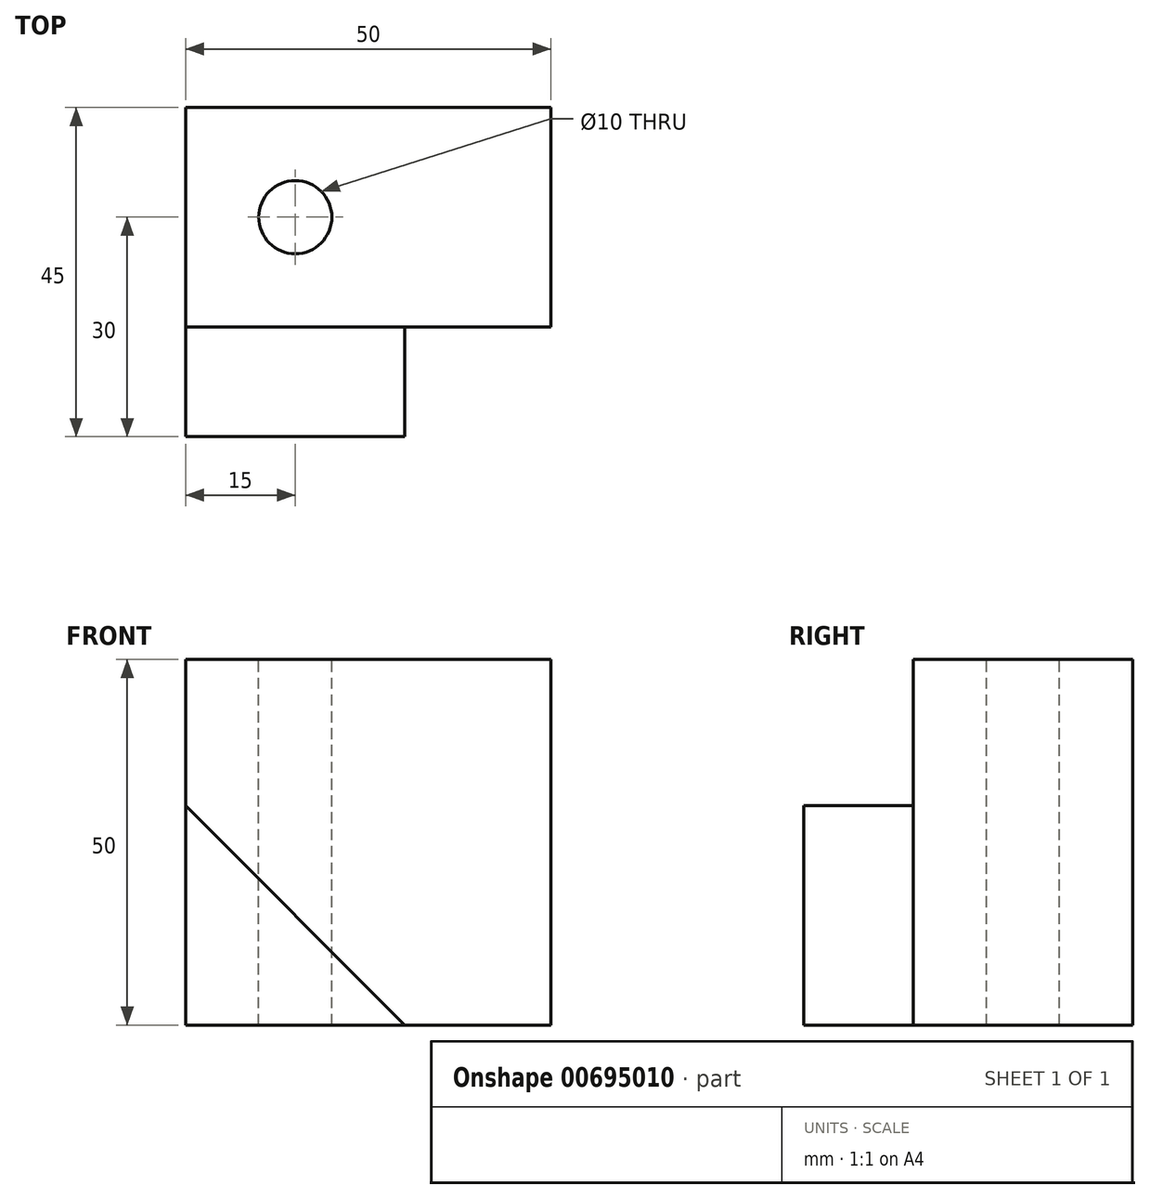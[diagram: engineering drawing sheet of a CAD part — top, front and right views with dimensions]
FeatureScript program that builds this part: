
annotation { "Feature Type Name" : "Feature", "Feature Type Description" : "" }
export const myFeature = defineFeature(function(context is Context, id is Id, definition is map)
    precondition{}
    {
        {
            var Q0;
            Q0=qCreatedBy(makeId("Front.planeOp"),FACE);
            var sketch = newSketch(context, id + "F0", { "sketchPlane" : qUnion([Q0])});
            skLineSegment(sketch, "E0", {"start": v(0, 0) * mm, "end": v(0, 30) * mm});
            skLineSegment(sketch, "E1", {"start": v(0, 0) * mm, "end": v(30, 0) * mm});
            skLineSegment(sketch, "E2", {"start": v(30, 0) * mm, "end": v(0, 30) * mm});
            skSolve(sketch);
        }
        {
            var Q0;
            Q0=makeQuery(id+"F0.imprint","IMPRINT",FACE,{"disambiguationData":[TD([[makeQuery(id+"F0.imprint","IMPRINT",EDGE,{"derivedFrom":sQuery(id+"F0.wireOp",EDGE,"E0")}),-1.0]])]});
            extrude(context, id + "F1", {"entities" : qUnion([Q0]), "oppositeDirection" : true, "depth" : 15 * mm, "offsetDistance" : 25 * mm});
        }
        {
            var Q0;
            Q0=qCreatedBy(makeId("Front.planeOp"),FACE);
            cPlane(context, id + "F2", {"entities" : qUnion([Q0]), "cplaneType" : CPlaneType.OFFSET, "offset" : 15 * mm, "oppositeDirection" : true, "width" : 150 * mm, "height" : 150 * mm});
        }
        {
            var Q0;
            Q0=qCreatedBy(id+"F2.planeOp",FACE);
            var sketch = newSketch(context, id + "F3", { "sketchPlane" : qUnion([Q0])});
            skLineSegment(sketch, "E3.bottom", {"start": v(0, 0) * mm, "end": v(50, 0) * mm});
            skLineSegment(sketch, "E3.top", {"start": v(0, 50) * mm, "end": v(50, 50) * mm});
            skLineSegment(sketch, "E3.left", {"start": v(0, 0) * mm, "end": v(0, 50) * mm});
            skLineSegment(sketch, "E3.right", {"start": v(50, 0) * mm, "end": v(50, 50) * mm});
            skSolve(sketch);
        }
        {
            var Q0;
            Q0 = qSketchRegion(id + "F3", true);
            extrude(context, id + "F4", {"entities" : qUnion([Q0]), "operationType" : NewBodyOperationType.ADD, "oppositeDirection" : true, "depth" : 30 * mm, "offsetDistance" : 25 * mm});
        }
        {
            var Q0;
            Q0=makeQuery(id+"F4.opExtrude","SWEPT_FACE",FACE,{"disambiguationData":[OSD([sQuery(id+"F3.wireOp",EDGE,"E3.top")])]});
            var sketch = newSketch(context, id + "F5", { "sketchPlane" : qUnion([Q0])});
            skCircle(sketch, "E4", {"center": v(15, 30) * mm, "radius": 5 * mm});
            skSolve(sketch);
        }
        {
            var Q0;
            Q0 = qSketchRegion(id + "F5", true);
            extrude(context, id + "F6", {"entities" : qUnion([Q0]), "operationType" : NewBodyOperationType.REMOVE, "endBound" : BoundingType.UP_TO_NEXT, "oppositeDirection" : true, "depth" : 25 * mm, "offsetDistance" : 25 * mm});
        }
    });
